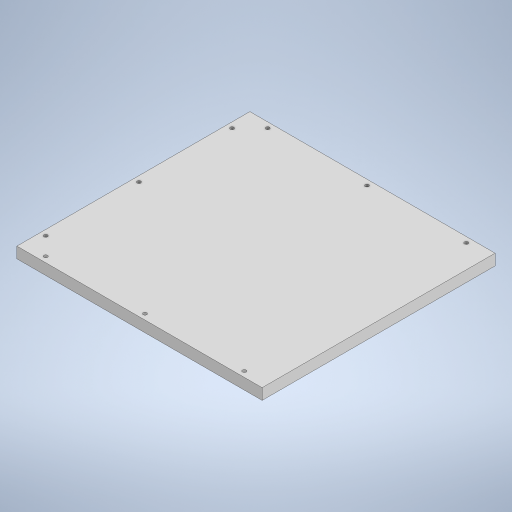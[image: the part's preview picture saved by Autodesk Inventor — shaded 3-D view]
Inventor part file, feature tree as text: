
AUTODESK INVENTOR PART (.ipt)
format: ipt  version: 2023.2 (Build 272271030, 271C)  size: 549,888 bytes
history: native  units: mm
features: extrude x3, sketch x2, projected_geometry x1
ambient origin geometry x8: Origin, YZ Plane, XZ Plane, XY Plane, X Axis, Y Axis, Z Axis, Center Point
bodies: Solid1 (feature_tree)
feature tree (6):
  extrude  "Extrusion1"  Depth=190.0mm
  sketch  "Sketch14"  dims[d2=9.0mm d3=0.0mm d47=9.0mm d48=9.0mm d49=9.0mm d50=3.0mm d51=3.0mm d52=3.0mm d53=10.0mm d54=0.0mm d55=3.0mm d56=3.0mm d57=3.0mm d58=10.0mm d59=0.0mm d60=19.0mm]
  extrude  "Extrusion14"  Depth=9.0mm
  extrude  "Extrusion15"  Depth=9.0mm
  sketch  "Sketch1"  dims[d0=200.0mm d1=190.0mm]
  projected_geometry  "Projected Loop12"
